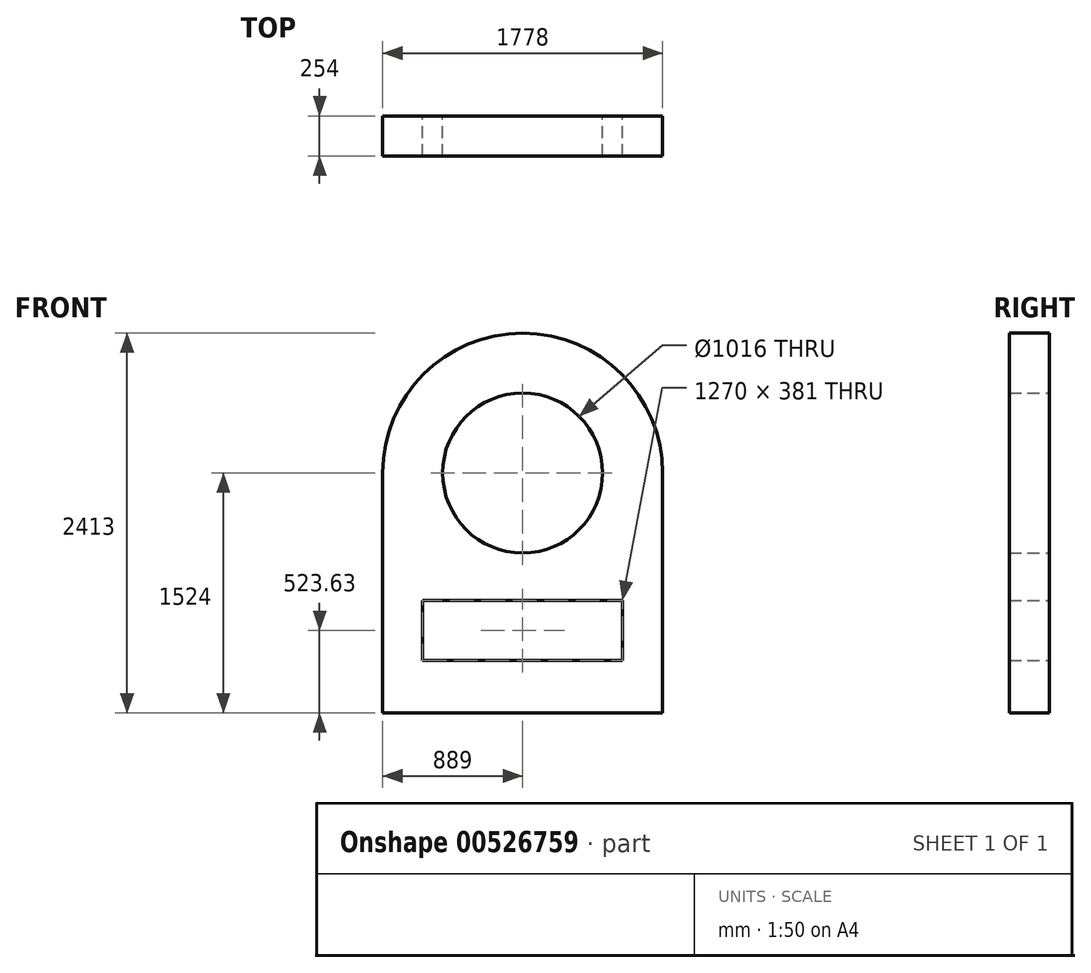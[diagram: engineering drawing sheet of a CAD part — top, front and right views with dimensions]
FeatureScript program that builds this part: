
annotation { "Feature Type Name" : "Feature", "Feature Type Description" : "" }
export const myFeature = defineFeature(function(context is Context, id is Id, definition is map)
    precondition{}
    {
        {
            var Q0;
            Q0=qCreatedBy(makeId("Front.planeOp"),FACE);
            var sketch = newSketch(context, id + "F0", { "sketchPlane" : qUnion([Q0])});
            skLineSegment(sketch, "E0", {"start": v(0, 0) * mm, "end": v(1778, 0) * mm});
            skLineSegment(sketch, "E1", {"start": v(1778, 0) * mm, "end": v(1778, 1524) * mm});
            skLineSegment(sketch, "E2", {"start": v(0, 0) * mm, "end": v(0, 1524) * mm});
            skLineSegment(sketch, "E3", {"start": v(254, 714.13) * mm, "end": v(254, 333.13) * mm});
            skLineSegment(sketch, "E4", {"start": v(254, 333.13) * mm, "end": v(1524, 333.13) * mm});
            skLineSegment(sketch, "E5", {"start": v(1524, 333.13) * mm, "end": v(1524, 714.13) * mm});
            skLineSegment(sketch, "E6", {"start": v(1524, 714.13) * mm, "end": v(254, 714.13) * mm});
            skArc(sketch, "E7", {"start": v(1778, 1524) * mm, "mid": v(889, 2413) * mm, "end": v(0, 1524) * mm});
            skCircle(sketch, "E8", {"center": v(889, 1524) * mm, "radius": 508 * mm});
            skSolve(sketch);
        }
        {
            var Q0;
            Q0 = qSketchRegion(id + "F0", true);
            extrude(context, id + "F1", {"entities" : qUnion([Q0]), "depth" : 254 * mm, "offsetDistance" : 25.4 * mm});
        }
    });
